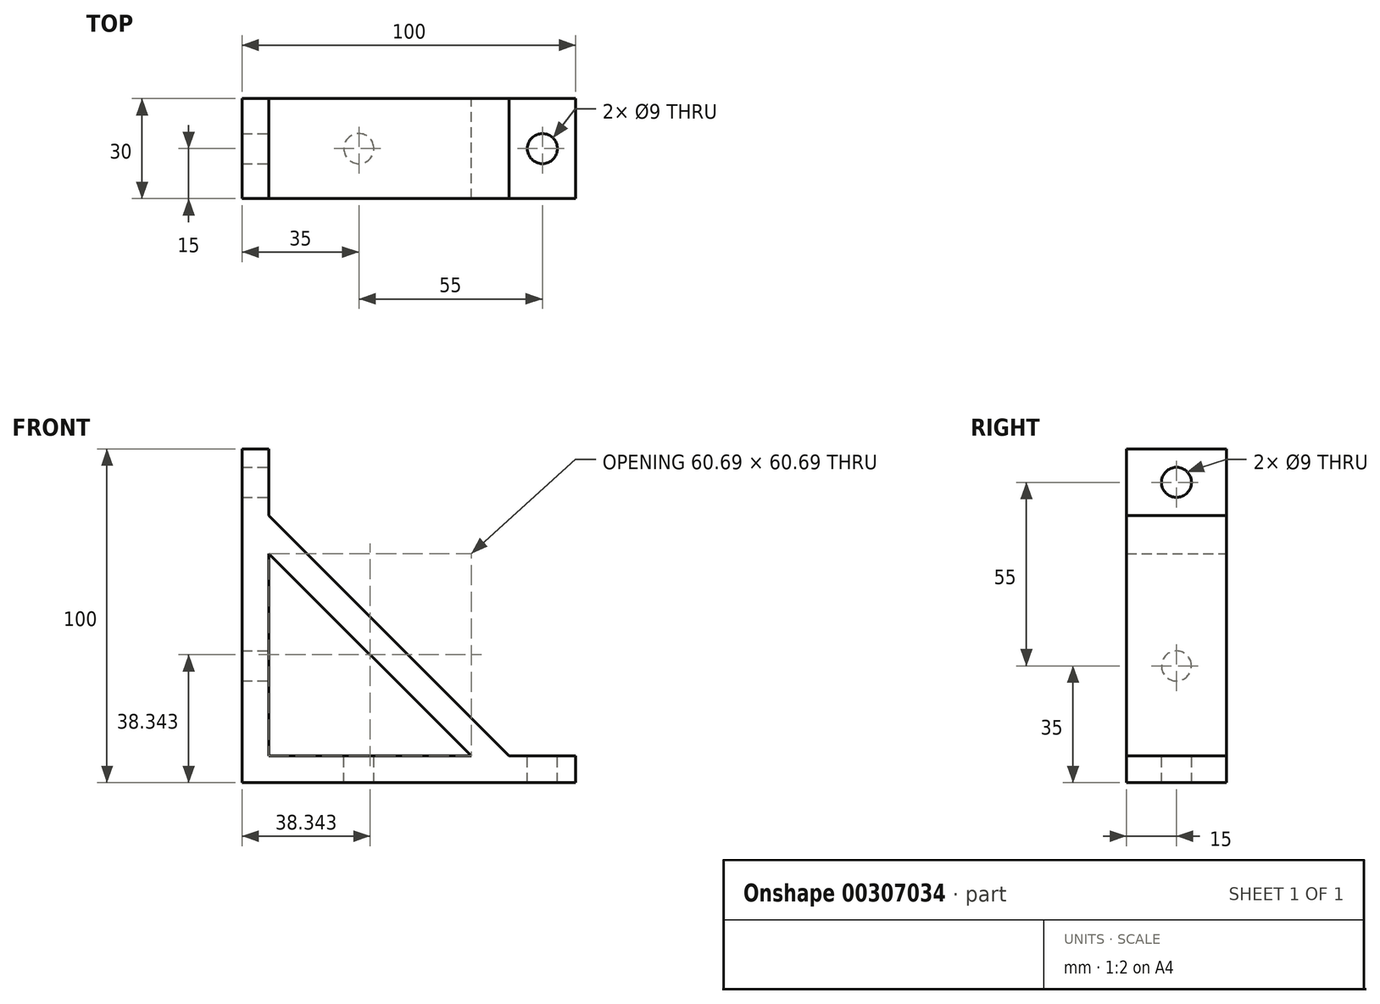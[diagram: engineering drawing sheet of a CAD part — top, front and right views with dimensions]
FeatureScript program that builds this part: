
annotation { "Feature Type Name" : "Feature", "Feature Type Description" : "" }
export const myFeature = defineFeature(function(context is Context, id is Id, definition is map)
    precondition{}
    {
        {
            var Q0;
            Q0=qCreatedBy(makeId("Front.planeOp"),FACE);
            var sketch = newSketch(context, id + "F0", { "sketchPlane" : qUnion([Q0])});
            skLineSegment(sketch, "E0", {"start": v(0, 0) * mm, "end": v(100, 0) * mm});
            skLineSegment(sketch, "E1", {"start": v(100, 0) * mm, "end": v(100, 8) * mm});
            skLineSegment(sketch, "E2", {"start": v(100, 8) * mm, "end": v(80, 8) * mm});
            skLineSegment(sketch, "E3", {"start": v(80, 8) * mm, "end": v(8, 80) * mm});
            skLineSegment(sketch, "E4", {"start": v(8, 80) * mm, "end": v(8, 100) * mm});
            skLineSegment(sketch, "E5", {"start": v(8, 100) * mm, "end": v(0, 100) * mm});
            skLineSegment(sketch, "E6", {"start": v(0, 100) * mm, "end": v(0, 0) * mm});
            skLineSegment(sketch, "E7", {"start": v(8, 68.69) * mm, "end": v(8, 8) * mm});
            skLineSegment(sketch, "E8", {"start": v(8, 68.69) * mm, "end": v(68.69, 8) * mm});
            skLineSegment(sketch, "E9", {"start": v(68.69, 8) * mm, "end": v(8, 8) * mm});
            skSolve(sketch);
        }
        {
            var Q0;
            Q0=makeQuery(id+"F0.imprint","IMPRINT",FACE,{"disambiguationData":[TD([[makeQuery(id+"F0.imprint","IMPRINT",EDGE,{"derivedFrom":sQuery(id+"F0.wireOp",EDGE,"E0")}),1.0]])]});
            extrude(context, id + "F1", {"entities" : qUnion([Q0]), "depth" : 30 * mm});
        }
        {
            var Q0;
            Q0=makeQuery(id+"F1.opExtrude","SWEPT_FACE",FACE,{"disambiguationData":[OSD([sQuery(id+"F0.wireOp",EDGE,"E2")])]});
            var sketch = newSketch(context, id + "F2", { "sketchPlane" : qUnion([Q0])});
            skLineSegment(sketch, "E10.0.0", {"start": v(100, 0) * mm, "end": v(80, 0) * mm});
            skLineSegment(sketch, "E10.0.1", {"start": v(80, 0) * mm, "end": v(80, -30) * mm});
            skLineSegment(sketch, "E10.0.2", {"start": v(80, -30) * mm, "end": v(100, -30) * mm});
            skLineSegment(sketch, "E10.0.3", {"start": v(100, -30) * mm, "end": v(100, 0) * mm});
            skLineSegment(sketch, "E11.0.0", {"start": v(68.69, 0) * mm, "end": v(8, 0) * mm});
            skLineSegment(sketch, "E11.0.1", {"start": v(8, 0) * mm, "end": v(8, -30) * mm});
            skLineSegment(sketch, "E11.0.2", {"start": v(8, -30) * mm, "end": v(68.69, -30) * mm});
            skLineSegment(sketch, "E11.0.3", {"start": v(68.69, -30) * mm, "end": v(68.69, 0) * mm});
            skPoint(sketch, "E12", {"position": v(90, -15) * mm});
            skPoint(sketch, "E13", {"position": v(35, -15) * mm});
            skSolve(sketch);
        }
        {
            var Q0;
            Q0=sQuery(id+"F2.wireOp",VERTEX,"E13");
            var Q1;
            Q1=sQuery(id+"F2.wireOp",VERTEX,"E12");
            var Q2;
            Q2=makeQuery(id+"F1.opExtrude","SWEPT_BODY",BODY,{"disambiguationData":[OSD([sQuery(id+"F0.wireOp",EDGE,"E0"),sQuery(id+"F0.wireOp",EDGE,"E1"),sQuery(id+"F0.wireOp",EDGE,"E2"),sQuery(id+"F0.wireOp",EDGE,"E3"),sQuery(id+"F0.wireOp",EDGE,"E4"),sQuery(id+"F0.wireOp",EDGE,"E5"),sQuery(id+"F0.wireOp",EDGE,"E6"),sQuery(id+"F0.wireOp",EDGE,"E7"),sQuery(id+"F0.wireOp",EDGE,"E8"),sQuery(id+"F0.wireOp",EDGE,"E9")])]});
            hole(context, id + "F3", {"style" : HoleStyle.SIMPLE, "endStyle" : HoleEndStyle.THROUGH, "holeDiameter" : 9 * mm, "tappedDepth" : 12 * mm, "tapClearance" : 3, "locations" : qUnion([Q0, Q1]), "scope" : qUnion([Q2])});
        }
        {
            var Q0;
            Q0=makeQuery(id+"F1.opExtrude","SWEPT_FACE",FACE,{"disambiguationData":[OSD([sQuery(id+"F0.wireOp",EDGE,"E4")])]});
            var sketch = newSketch(context, id + "F4", { "sketchPlane" : qUnion([Q0])});
            skLineSegment(sketch, "E14.0.0", {"start": v(0, 80) * mm, "end": v(0, 100) * mm});
            skLineSegment(sketch, "E14.0.1", {"start": v(0, 100) * mm, "end": v(-30, 100) * mm});
            skLineSegment(sketch, "E14.0.2", {"start": v(-30, 100) * mm, "end": v(-30, 80) * mm});
            skLineSegment(sketch, "E14.0.3", {"start": v(-30, 80) * mm, "end": v(0, 80) * mm});
            skLineSegment(sketch, "E15.0.0", {"start": v(0, 8) * mm, "end": v(0, 68.69) * mm});
            skLineSegment(sketch, "E15.0.1", {"start": v(0, 68.69) * mm, "end": v(-30, 68.69) * mm});
            skLineSegment(sketch, "E15.0.2", {"start": v(-30, 68.69) * mm, "end": v(-30, 8) * mm});
            skLineSegment(sketch, "E15.0.3", {"start": v(-30, 8) * mm, "end": v(0, 8) * mm});
            skPoint(sketch, "E16", {"position": v(-15, 90) * mm});
            skPoint(sketch, "E17", {"position": v(-15, 35) * mm});
            skSolve(sketch);
        }
        {
            var Q0;
            Q0=sQuery(id+"F4.wireOp",VERTEX,"E16");
            var Q1;
            Q1=sQuery(id+"F4.wireOp",VERTEX,"E17");
            var Q2;
            Q2=makeQuery(id+"F1.opExtrude","SWEPT_BODY",BODY,{"disambiguationData":[OSD([sQuery(id+"F0.wireOp",EDGE,"E0"),sQuery(id+"F0.wireOp",EDGE,"E1"),sQuery(id+"F0.wireOp",EDGE,"E2"),sQuery(id+"F0.wireOp",EDGE,"E3"),sQuery(id+"F0.wireOp",EDGE,"E4"),sQuery(id+"F0.wireOp",EDGE,"E5"),sQuery(id+"F0.wireOp",EDGE,"E6"),sQuery(id+"F0.wireOp",EDGE,"E7"),sQuery(id+"F0.wireOp",EDGE,"E8"),sQuery(id+"F0.wireOp",EDGE,"E9")])]});
            hole(context, id + "F5", {"style" : HoleStyle.SIMPLE, "endStyle" : HoleEndStyle.THROUGH, "holeDiameter" : 9 * mm, "tappedDepth" : 12 * mm, "tapClearance" : 3, "locations" : qUnion([Q0, Q1]), "scope" : qUnion([Q2])});
        }
    });
